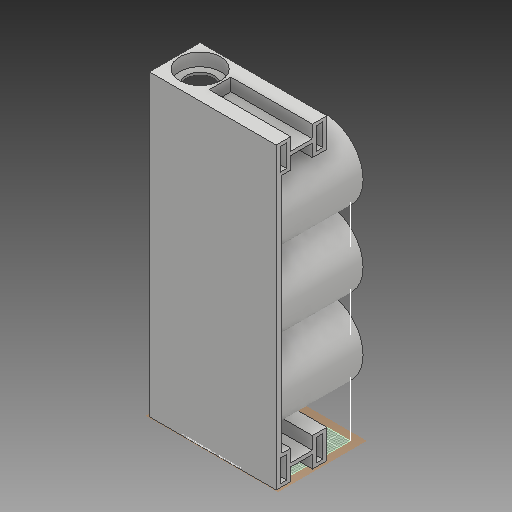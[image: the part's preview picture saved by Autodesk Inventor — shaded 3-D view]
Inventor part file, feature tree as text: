
AUTODESK INVENTOR PART (.ipt)
format: ipt  version: 2018 (Build 220112000, 112)  size: 738,304 bytes
history: native  units: mm
features: sketch x23, extrude x20, fillet x4
ambient origin geometry x8: Origin, YZ Plane, XZ Plane, XY Plane, X Axis, Y Axis, Z Axis, Center Point
bodies: Solid1 (feature_tree)
feature tree (47):
  extrude  "Extrusion1"  Depth=165.0mm
  extrude  "Extrusion2"  Depth=8.5mm
  extrude  "Extrusion3"  Depth=25.0mm TaperAngle=0.0deg
  extrude  "Extrusion4"  Depth=22.75mm
  extrude  "Extrusion5"  Depth=15.5mm
  extrude  "Extrusion6"  Depth=7.1mm TaperAngle=0.0deg
  fillet  "Fillet1"  Radius=5.0mm
  extrude  "Extrusion7"  Depth=10.0mm TaperAngle=0.0deg
  fillet  "Fillet2"  Radius=2.0mm
  extrude  "Extrusion8"  Depth=16.0mm
  extrude  "Extrusion9"  Depth=16.0mm
  fillet  "Fillet3"  Radius=8.0mm
  extrude  "Extrusion10"  Depth=6.0mm
  extrude  "Extrusion11"  Depth=12.25mm
  sketch  "Sketch12"  dims[d32=12.25mm d33=3.5mm]
  sketch  "Sketch13"  dims[d34=12.25mm d35=12.25mm]
  extrude  "Extrusion12"  Depth=12.25mm
  extrude  "Extrusion13"  Depth=12.25mm
  sketch  "Sketch16"  dims[d41=8.0mm d42=1.0mm]
  extrude  "Extrusion14"  Depth=40.0mm TaperAngle=0.0deg
  extrude  "Extrusion15"  Depth=2.0mm
  extrude  "Extrusion16"  Depth=1.0mm
  extrude  "Extrusion17"  Depth=2.0mm TaperAngle=0.0deg
  extrude  "Extrusion18"  Depth=7.1mm TaperAngle=0.0deg
  fillet  "Fillet4"  Radius=3.0mm
  extrude  "Extrusion19"  Depth=42.0mm
  extrude  "Extrusion20"  Depth=42.0mm
  sketch  "Sketch1"  dims[d0=25.0mm d1=165.0mm]
  sketch  "Sketch2"  dims[d2=3.0mm d3=0.0mm d4=8.5mm]
  sketch  "Sketch3"  dims[d5=8.5mm d6=25.0mm d7=0.0mm]
  sketch  "Sketch4"  dims[d8=25.0mm d9=22.75mm]
  sketch  "Sketch5"  dims[d10=7.1mm d11=0.0mm d12=15.5mm]
  sketch  "Sketch6"  dims[d13=165.0mm d14=0.0mm d15=7.1mm d16=0.0mm d17=5.0mm]
  sketch  "Sketch7"  dims[d18=5.0mm d19=10.0mm d20=0.0mm d21=2.0mm]
  sketch  "Sketch8"  dims[d22=16.0mm d23=8.0mm]
  sketch  "Sketch9"  dims[d24=16.0mm d25=16.0mm d26=8.0mm]
  sketch  "Sketch10"  dims[d27=45.0mm d28=0.0mm d29=6.0mm]
  sketch  "Sketch11"  dims[d30=12.25mm d31=3.5mm]
  sketch  "Sketch14"  dims[d36=3.5mm d37=40.0mm d38=0.0mm]
  sketch  "Sketch15"  dims[d39=1.0mm d40=2.0mm]
  sketch  "Sketch17"  dims[d43=2.0mm d44=12.0mm d45=0.0mm]
  sketch  "Sketch18"  dims[d46=6.0mm d47=7.1mm d48=0.0mm d49=3.0mm d50=0.0mm]
  sketch  "Sketch19"  dims[d51=42.0mm d52=38.75mm]
  sketch  "Sketch20"  dims[d53=42.0mm d54=38.75mm]
  sketch  "Sketch21"  dims[d55=42.0mm]
  sketch  "Sketch22"  dims[d56=38.75mm]
  sketch  "Sketch23"  dims[d57=45.0mm d58=0.0mm d59=2.0mm d60=4.0mm d61=2.0mm d62=4.0mm d63=45.0mm d64=0.0mm d65=10.0mm d66=12.0mm d67=0.0mm d68=2.0mm d69=0.0mm d70=2.0mm d71=0.0mm d72=2.0mm d73=2.0mm d74=5.0mm d75=0.0mm d76=2.0mm d77=2.0mm d78=7.0mm d79=0.0mm d80=1.0mm d81=0.25mm d82=0.25mm d83=44.75mm d84=0.0mm d85=44.0mm d86=0.0mm]
